# Revit family: HVAC_Heaters_Enertech_CTC-EcoZenith-i255H
name_source: partatom
category: Specialty Equipment
revit_build: Autodesk Revit 2017 (Build: 20190508_0315(x64)
units: mm (PartAtom-declared; Revit-internal decimal feet)

## family parameters
Always vertical = Yes
Cut with Voids When Loaded = No
OmniClass Number = 23.75.00.00
OmniClass Title = Climate Control (HVAC)
Part Type = Normal
Room Calculation Point = No
Round Connector Dimension = Use Diameter
Shared = No
Work Plane-Based = No

## types (1)
- CTC EcoZenith i255 H - 400V3N
    AssetType = Fixed
    BIMObjectName = HVAC_Heaters_Enertech_CTC-EcoZenith-i255
    Brand = CTC
    Category = Indoor Module
    Color = white
    ConnectorDistance1 = 86 mm
    ConnectorDistance2 = 144 mm  [stored 0.472441 ft]
    ConnectorDistance3 = 5 mm  [stored 0.0164042 ft]
    ConvergoRefNr = 0091-1710-0012-SE
    Cost = 0 $
    Description = Quiet and efficient indoor module available in two heights with built-in heat pump control and hot water preparation. The CTC EcoZenith i255  has internet connection as standard, so you can easily control your product remotely. It is also prepared for connection to Alexa and Google Home, etc.
    DurationUnit = Year
    EANNumber = 7333077094461
    ElectricalDeviceNominalPower = 1800 W
    EnergyClassHeatingWithControl = A++ / A++ (with heatpump)
    EnergyClass_HotWater_TapProfile = B / L
    GroupFuse = 15 kW : 25 A
18 kW: 32 A
    HasProtectiveEarth = Yes
    HotTapWaterPerformance = 173 liters
    IP_Code = IP X1
    IfcExportAs = IfcElectricalDeviceCommon
    IfcExportType = HEATER
    Manufacturer = Enertech AB
    ManufacturerCountry = Sweden
    ManufacturerName = Enertech AB
    ManufacturerURL = https://ctc.se
    Material = Steel/copper
    MaxOperatingPressureHotWater = 10 bar
    MaxOperatingPressureThermalStore = 3 bar
    MinimumCeilingHeight = 1901 mm
    Model = CTC EcoZenith i250 High
    ModelNumber = 589502001
    ModelType = EcoZenithI250-high : EcoZenith_high
    NBSDescription = Air to water heat pumps
    NBSReference = 90-40-40/320
    Name = CTC-EcoZenith-i255
    NominalCurrent = 0 A
    NominalDepth = 672 mm  [stored 2.20472 ft]
    NominalFrequencyRange = 50 Hz
    NominalHeight = 1904 mm  [stored 6.24672 ft]
    NominalVoltage = 400 V
    NominalWidth = 595 mm  [stored 1.9521 ft]
    OutputRangeIimmersionHeater = 0.3 - 15/ 0.3 - 18
    PhaseAngle = 0.00°
    PowerFactor = 0 W
    ProductInformation = Quiet and efficient indoor module available in two heights with built-in heat pump control and hot water preparation. The CTC EcoZenith i255  has internet connection as standard, so you can easily control your product remotely. It is also prepared for connection to Alexa and Google Home, etc.
    PumpMainMaterial = Stainless Steel
    RatedHeatOutputModerate = 15 kW
    RatedVoltage = 1200 V
    Revision = 4
    Shape = Rectangular
    Size = 673x596x1886 mm
    Touchscreen = yes
    UNSPSCCode = 40102003
    URL = https://ctc-heating.com
    Uniclass2 = Pr_40_70_65
    Uniclass2015Description = Preparation catering equipment
    Uniclass2015Reference = Pr_40_70_65
    UsageCurrent = 0 A
    Version = 1
    VersionDate = 10/11/2020
    WarrantyDurationUnit = Year
    WaterVolumeHeathingSystem = 223 liters
    WaterVolumeWaterSuply = 5.7 liters
    Weight = 182 kg

note: [stored X ft] marks values corroborated as IEEE doubles in the binary element streams (Revit-internal decimal feet)

## geometry (parser evidence)
native form markers: Sweep x4
no freeform markers — native parametric forms only
